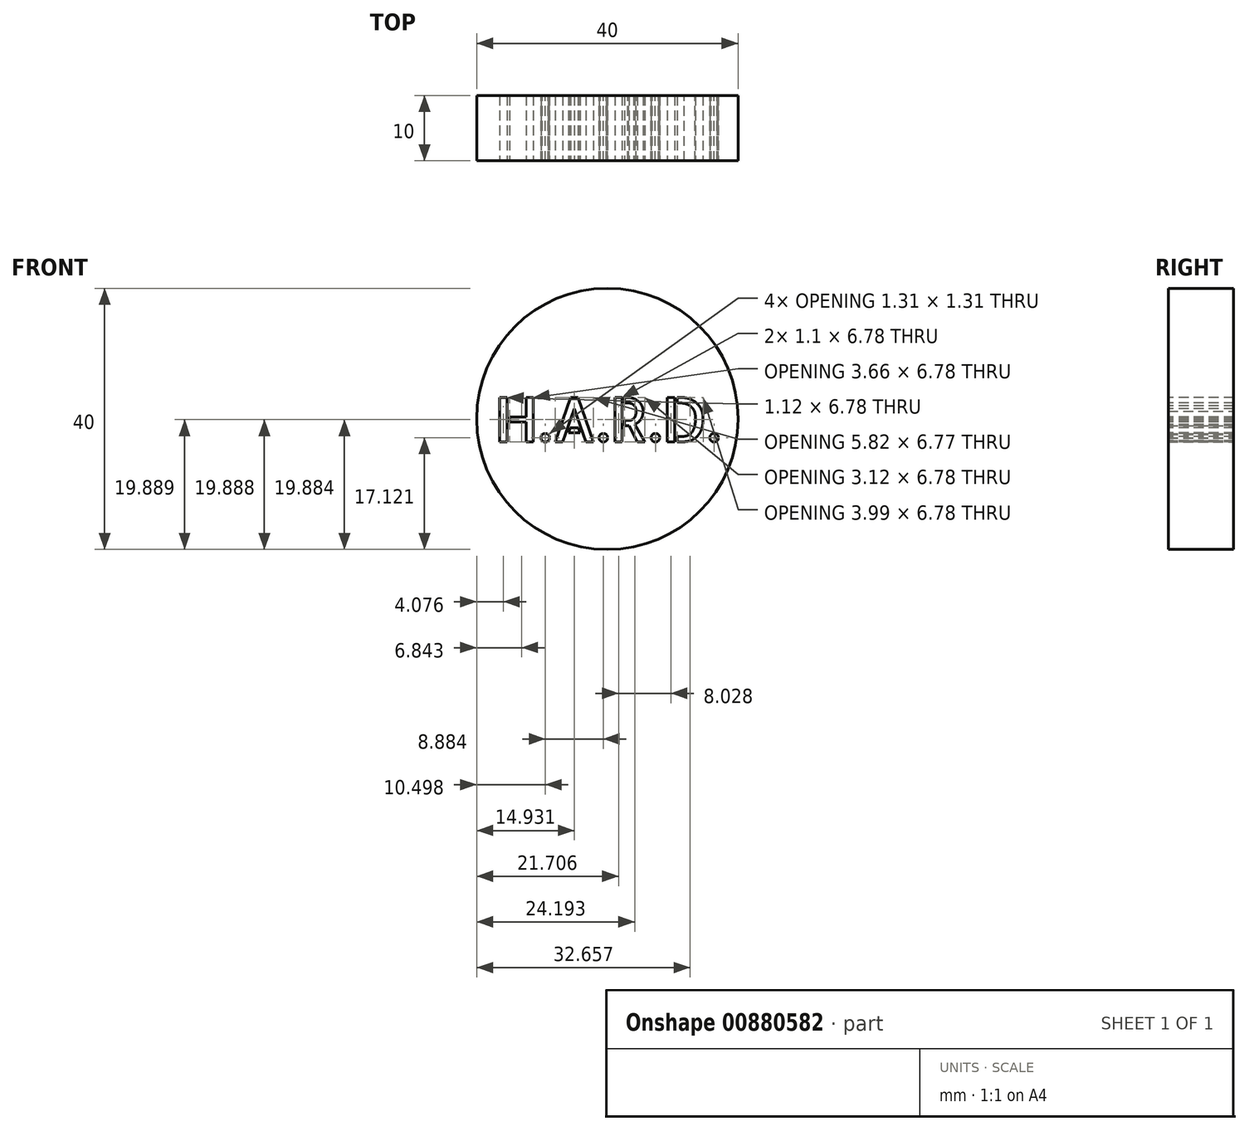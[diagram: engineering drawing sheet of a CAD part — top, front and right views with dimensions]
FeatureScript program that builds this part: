
annotation { "Feature Type Name" : "Feature", "Feature Type Description" : "" }
export const myFeature = defineFeature(function(context is Context, id is Id, definition is map)
    precondition{}
    {
        {
            var Q0;
            Q0=qCreatedBy(makeId("Front.planeOp"),FACE);
            var sketch = newSketch(context, id + "F0", { "sketchPlane" : qUnion([Q0])});
            skCircle(sketch, "E0", {"center": v(0, 0) * mm, "radius": 20 * mm});
            skSolve(sketch);
        }
        {
            var Q0;
            Q0=makeQuery(id+"F0.imprint","IMPRINT",FACE,{"disambiguationData":[TD([[makeQuery(id+"F0.imprint","IMPRINT",EDGE,{"derivedFrom":sQuery(id+"F0.wireOp",EDGE,"E0")}),1.0]])]});
            extrude(context, id + "F1", {"entities" : qUnion([Q0]), "depth" : 10 * mm, "offsetDistance" : 25 * mm});
        }
        {
            var Q0;
            Q0=makeQuery(id+"F1.opExtrude","CAP_FACE",FACE,{"disambiguationData":[OSD([sQuery(id+"F0.wireOp",EDGE,"E0")])],"isStart":false});
            var sketch = newSketch(context, id + "F2", { "sketchPlane" : qUnion([Q0])});
            skText(sketch, "E1", { "text": "H.A.R.D.\n", "fontName": "AllertaStencil-Regular.ttf"});
            const initialGuessF2  = {"E1": [-0.01735, -0.0035, 1, 0, 0.00678]};
            skSetInitialGuess(sketch, initialGuessF2);
            skSolve(sketch);
        }
        {
            var Q0;
            Q0 = qSketchRegion(id + "F2", true);
            extrude(context, id + "F3", {"entities" : qUnion([Q0]), "operationType" : NewBodyOperationType.REMOVE, "oppositeDirection" : true, "depth" : 10 * mm, "offsetDistance" : 25 * mm});
        }
    });
